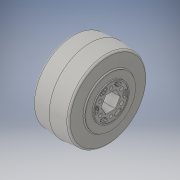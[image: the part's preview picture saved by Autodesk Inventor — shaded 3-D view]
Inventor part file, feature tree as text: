
AUTODESK INVENTOR PART (.ipt)
format: ipt  version: 2016 (Build 200138000, 138)  size: 1,963,008 bytes
history: native  units: in
note: dims shown in document units (in); Inventor stores cm internally (conversion verified against a paired STEP export)
features: revolve x1
ambient origin geometry x8: Origin, YZ Plane, XZ Plane, XY Plane, X Axis, Y Axis, Z Axis, Center Point
bodies: Solid1 (feature_tree)
feature tree (1):
  revolve  "Revolve1"  [1 undecoded]
note: 1 required parameter value undecoded (feature->parameter linkage not recoverable at this tier; creation-order binding heuristic only, values carry confidence <= 0.55)
